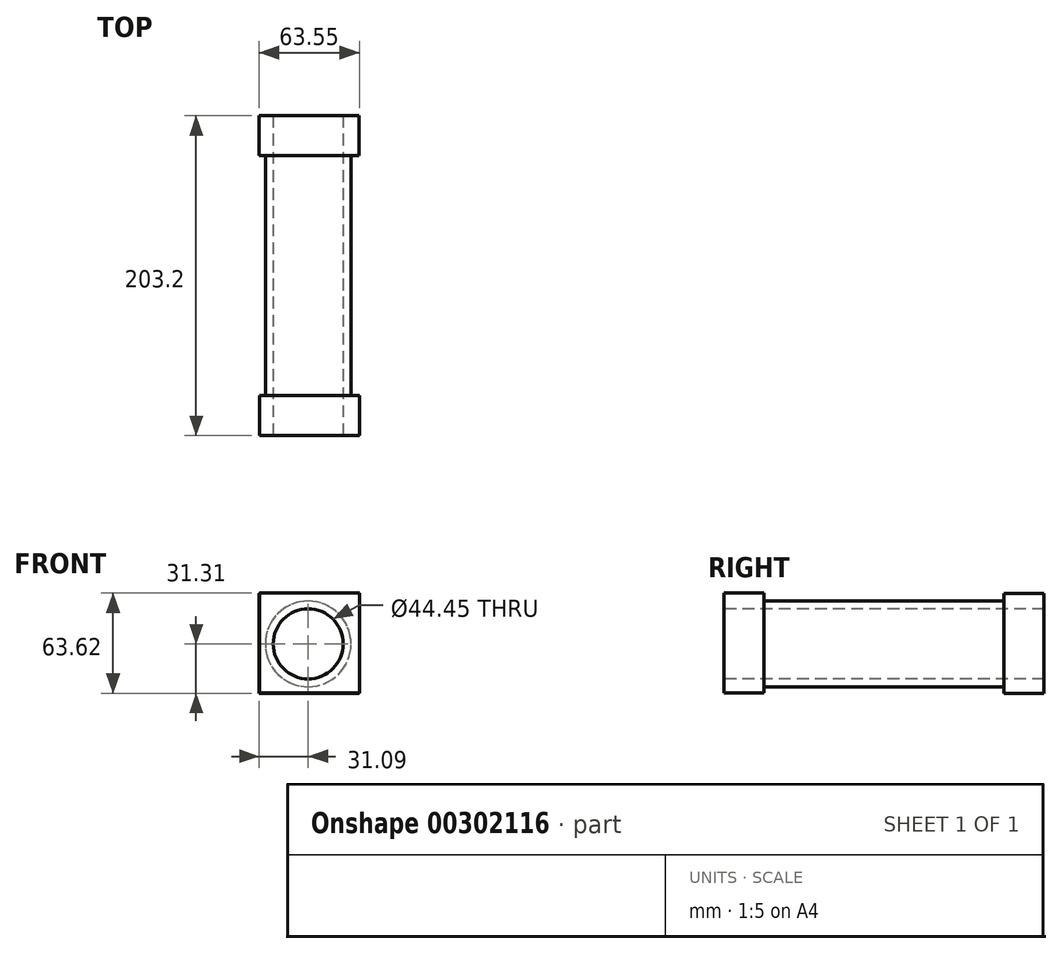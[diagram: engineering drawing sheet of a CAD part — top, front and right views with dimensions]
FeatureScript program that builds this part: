
annotation { "Feature Type Name" : "Feature", "Feature Type Description" : "" }
export const myFeature = defineFeature(function(context is Context, id is Id, definition is map)
    precondition{}
    {
        {
            var Q0;
            Q0=qCreatedBy(makeId("Front.planeOp"),FACE);
            var sketch = newSketch(context, id + "F0", { "sketchPlane" : qUnion([Q0])});
            skCircle(sketch, "E0", {"center": v(0, 0) * mm, "radius": 27.23 * mm});
            skSolve(sketch);
        }
        {
            var Q0;
            Q0=makeQuery(id+"F0.imprint","IMPRINT",FACE,{"disambiguationData":[TD([[makeQuery(id+"F0.imprint","IMPRINT",EDGE,{"derivedFrom":sQuery(id+"F0.wireOp",EDGE,"E0")}),1.0]])]});
            extrude(context, id + "F1", {"entities" : qUnion([Q0]), "depth" : 101.6 * mm, "hasSecondDirection" : true, "secondDirectionOppositeDirection" : true, "secondDirectionDepth" : 101.6 * mm});
        }
        {
            var Q0;
            Q0=makeQuery(id+"F1.opExtrude","CAP_FACE",FACE,{"disambiguationData":[OSD([sQuery(id+"F0.wireOp",EDGE,"E0")])],"isStart":false});
            var sketch = newSketch(context, id + "F2", { "sketchPlane" : qUnion([Q0])});
            skLineSegment(sketch, "E1.bottom", {"start": v(-31.04, 32.31) * mm, "end": v(32.46, 32.31) * mm});
            skLineSegment(sketch, "E1.top", {"start": v(-31.04, -31.19) * mm, "end": v(32.46, -31.19) * mm});
            skLineSegment(sketch, "E1.left", {"start": v(-31.04, 32.31) * mm, "end": v(-31.04, -31.19) * mm});
            skLineSegment(sketch, "E1.right", {"start": v(32.46, 32.31) * mm, "end": v(32.46, -31.19) * mm});
            skSolve(sketch);
        }
        {
            var Q0;
            Q0=makeQuery(id+"F2.imprint","IMPRINT",FACE,{"disambiguationData":[TD([[makeQuery(id+"F2.imprint","IMPRINT",EDGE,{"derivedFrom":sQuery(id+"F2.wireOp",EDGE,"E1.bottom")}),-1.0]])]});
            extrude(context, id + "F3", {"entities" : qUnion([Q0]), "operationType" : NewBodyOperationType.ADD, "oppositeDirection" : true, "depth" : 25.4 * mm});
        }
        {
            var Q0;
            Q0=makeQuery(id+"F1.opExtrude","CAP_FACE",FACE,{"disambiguationData":[OSD([sQuery(id+"F0.wireOp",EDGE,"E0")])],"isStart":false});
            var sketch = newSketch(context, id + "F4", { "sketchPlane" : qUnion([Q0])});
            skCircle(sketch, "E2", {"center": v(0, 0) * mm, "radius": 22.23 * mm});
            skSolve(sketch);
        }
        {
            var Q0;
            Q0=makeQuery(id+"F1.opExtrude","CAP_FACE",FACE,{"disambiguationData":[OSD([sQuery(id+"F0.wireOp",EDGE,"E0")])],"isStart":true});
            var sketch = newSketch(context, id + "F5", { "sketchPlane" : qUnion([Q0])});
            skLineSegment(sketch, "E3.bottom", {"start": v(-32.41, 32.2) * mm, "end": v(31.09, 32.2) * mm});
            skLineSegment(sketch, "E3.top", {"start": v(-32.41, -31.3) * mm, "end": v(31.09, -31.3) * mm});
            skLineSegment(sketch, "E3.left", {"start": v(-32.41, 32.2) * mm, "end": v(-32.41, -31.3) * mm});
            skLineSegment(sketch, "E3.right", {"start": v(31.09, 32.2) * mm, "end": v(31.09, -31.3) * mm});
            skSolve(sketch);
        }
        {
            var Q0;
            Q0 = qSketchRegion(id + "F5", true);
            extrude(context, id + "F6", {"entities" : qUnion([Q0]), "operationType" : NewBodyOperationType.ADD, "oppositeDirection" : true, "depth" : 25.4 * mm});
        }
        {
            var Q0;
            Q0=makeQuery(id+"F4.imprint","IMPRINT",FACE,{"disambiguationData":[TD([[makeQuery(id+"F4.imprint","IMPRINT",EDGE,{"derivedFrom":sQuery(id+"F4.wireOp",EDGE,"E2")}),1.0]])]});
            extrude(context, id + "F7", {"entities" : qUnion([Q0]), "operationType" : NewBodyOperationType.REMOVE, "oppositeDirection" : true, "depth" : 203.2 * mm});
        }
    });
